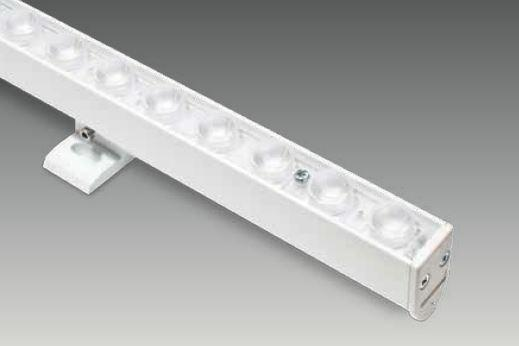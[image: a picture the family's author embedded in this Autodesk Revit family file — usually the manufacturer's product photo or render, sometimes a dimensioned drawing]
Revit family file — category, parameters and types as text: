
# Revit family: SD 1200 RUB
name_source: partatom
category: Lighting Fixtures
revit_build: Autodesk Revit 2017 (Build: 20160225_1515(x64)
units: mm (PartAtom-declared; Revit-internal decimal feet)

## family parameters
Cut with Voids When Loaded = No
Host = Face
Light Source = Yes
Part Type = Normal
Room Calculation Point = No
Round Connector Dimension = Use Diameter
Shared = No

## types (3) — shared parameters
Apparent Load = 44 VA
Color Filter = 16777215
Default Elevation = 1219 mm
Dimming Lamp Color Temperature Shift = <None>
Emit Shape Visible in Rendering = Yes
Emit from Rectangle Length = 20 mm  [stored 0.0656168 ft]
Emit from Rectangle Width = 1190 mm  [stored 3.9042 ft]
Light Source Symbol Size = 610 mm
Manufacturer = ARLIGHT
Type Image = SD 1200 RUB.JPG
Wattage Comments = 44W

## per-type parameters (varying)
| type | Beam Angle |
| SDRUB.1200.27.44.30 | 27.00° |
| SDRUB.1200.38.44.30 | 38.00° |
| SDRUB.1200.4520.44.30 | 20.00° |

note: [stored X ft] marks values corroborated as IEEE doubles in the binary element streams (Revit-internal decimal feet)

## geometry (parser evidence)
native form markers: Sweep x3
no freeform markers — native parametric forms only
